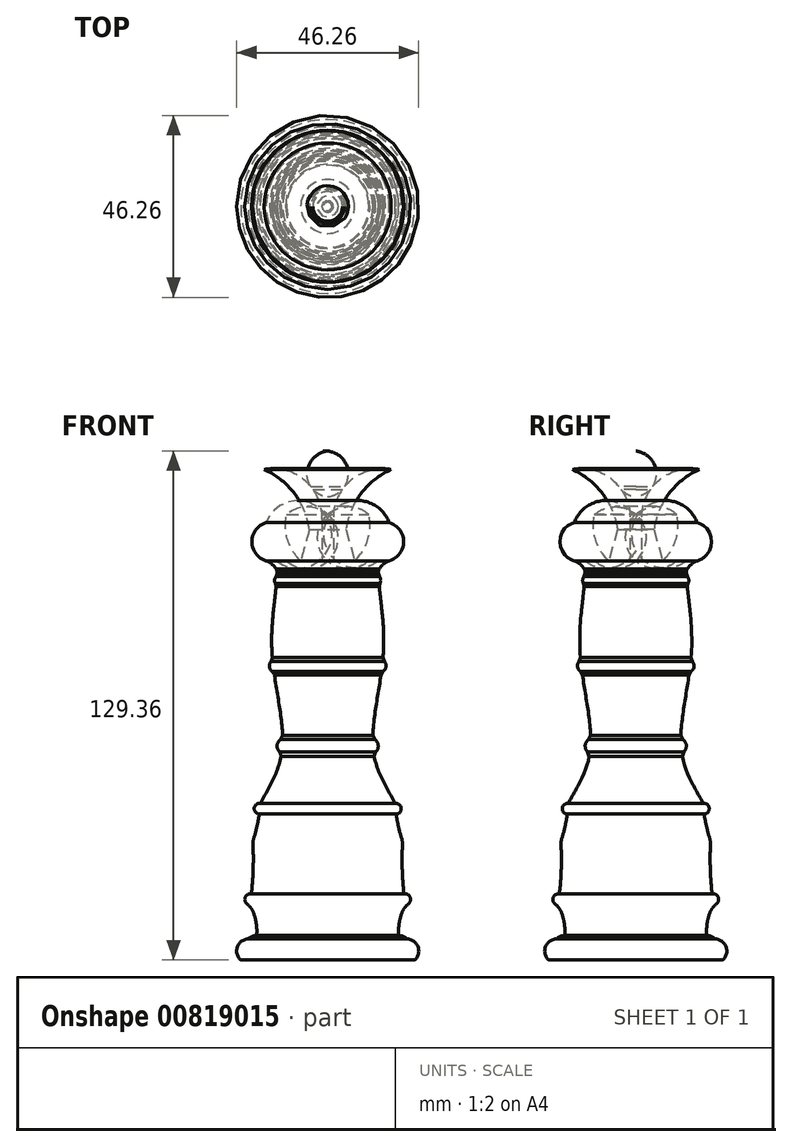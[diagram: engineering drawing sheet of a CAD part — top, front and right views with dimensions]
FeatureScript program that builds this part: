
annotation { "Feature Type Name" : "Feature", "Feature Type Description" : "" }
export const myFeature = defineFeature(function(context is Context, id is Id, definition is map)
    precondition{}
    {
        {
            var Q0;
            Q0=qCreatedBy(makeId("Front.planeOp"),FACE);
            var sketch = newSketch(context, id + "F0", { "sketchPlane" : qUnion([Q0])});
            skLineSegment(sketch, "E0", {"start": v(0, -37.92) * mm, "end": v(0, 57.3) * mm});
            skArc(sketch, "E1", {"start": v(-11.45, 12.13) * mm, "mid": v(-12.85, 10.36) * mm, "end": v(-11.68, 8.42) * mm});
            skArc(sketch, "E2", {"start": v(-14, 32.07) * mm, "mid": v(-14.81, 30.39) * mm, "end": v(-13.62, 28.94) * mm});
            skArc(sketch, "E3", {"start": v(-19.74, -30.2) * mm, "mid": v(-18.98, -22.08) * mm, "end": v(-19.03, -13.92) * mm});
            skFitSpline(sketch, "E4.trimOffspring", {"points": [v(-25.61, -37.92) * mm, v(-19.46, -8.96) * mm, v(-11.68, 8.42) * mm, v(-14.2, 35.39) * mm, v(-12.94, 57.3) * mm, v(-15.84, 63.8) * mm], "startDerivative": vector(16.77, 129.7) * mm, "endDerivative": vector(-31.89, 45.75) * mm});
            skArc(sketch, "E5", {"start": v(-19.03, -13.92) * mm, "mid": v(-17.75, -9.2) * mm, "end": v(-17.15, -4.34) * mm});
            skArc(sketch, "E6", {"start": v(-18.05, -37.92) * mm, "mid": v(-18.31, -33.93) * mm, "end": v(-19.74, -30.2) * mm});
            skArc(sketch, "E7", {"start": v(-17.15, -4.34) * mm, "mid": v(-18.67, -5.58) * mm, "end": v(-17.4, -7.09) * mm});
            skArc(sketch, "E8", {"start": v(-19.38, -27.31) * mm, "mid": v(-21.06, -28.56) * mm, "end": v(-19.74, -30.2) * mm});
            skArc(sketch, "E9", {"start": v(-18.05, -37.92) * mm, "mid": v(-21.18, -41.05) * mm, "end": v(-18.05, -44.17) * mm});
            skArc(sketch, "E10", {"start": v(-20.2, -38.78) * mm, "mid": v(-22.96, -40.84) * mm, "end": v(-22.07, -44.17) * mm});
            skLineSegment(sketch, "E11", {"start": v(-18.05, -44.17) * mm, "end": v(0, -44.17) * mm});
            skLineSegment(sketch, "E12", {"start": v(0, -44.17) * mm, "end": v(0, -37.92) * mm});
            skLineSegment(sketch, "E13", {"start": v(-18.05, -44.17) * mm, "end": v(-22.07, -44.17) * mm});
            skPoint(sketch, "E14.orphan", {"position": v(0, 63.8) * mm});
            skArc(sketch, "E15", {"start": v(-12.4, 50.83) * mm, "mid": v(-12.77, 54.68) * mm, "end": v(-15.62, 57.3) * mm});
            skLineSegment(sketch, "E16", {"start": v(-12.4, 50.83) * mm, "end": v(-13.67, 45.68) * mm});
            skPoint(sketch, "E16.startSnap0", {"position": v(-12.4, 53.75) * mm});
            skArc(sketch, "E17", {"start": v(-12.4, 53.75) * mm, "mid": v(-13.49, 52.3) * mm, "end": v(-12.4, 50.83) * mm});
            skArc(sketch, "E18", {"start": v(-15.62, 66.98) * mm, "mid": v(-19.28, 62.14) * mm, "end": v(-15.62, 57.3) * mm});
            skArc(sketch, "E19", {"start": v(-15.62, 66.98) * mm, "mid": v(-15.84, 61.7) * mm, "end": v(-12.94, 57.3) * mm});
            skLineSegment(sketch, "E20", {"start": v(0, 67.93) * mm, "end": v(0, 57.3) * mm});
            skLineSegment(sketch, "E21.trimOffspring", {"start": v(-7.95, 57.3) * mm, "end": v(0, 57.3) * mm});
            skLineSegment(sketch, "E22", {"start": v(-12.94, 57.3) * mm, "end": v(-7.95, 57.3) * mm});
            skArc(sketch, "E23", {"start": v(-10.44, 69.01) * mm, "mid": v(-13.06, 63.15) * mm, "end": v(-10.44, 57.3) * mm});
            skPoint(sketch, "E23.startSnap0", {"position": v(-10.44, 57.3) * mm});
            skArc(sketch, "E24", {"start": v(-10.44, 69.01) * mm, "mid": v(-10.21, 62.68) * mm, "end": v(-6.86, 57.3) * mm});
            skArc(sketch, "E25", {"start": v(-1.43, 67.73) * mm, "mid": v(-5.73, 77.63) * mm, "end": v(-16.14, 80.49) * mm});
            skArc(sketch, "E26", {"start": v(-4.64, 65.2) * mm, "mid": v(-8.41, 74.33) * mm, "end": v(-16.14, 80.49) * mm});
            skArc(sketch, "E27", {"start": v(0, 85.16) * mm, "mid": v(-5.24, 79.36) * mm, "end": v(0, 73.56) * mm});
            skLineSegment(sketch, "E28", {"start": v(0, 85.16) * mm, "end": v(0, 73.56) * mm});
            skLineSegment(sketch, "E29", {"start": v(-4.64, 65.2) * mm, "end": v(-6.86, 57.3) * mm});
            skLineSegment(sketch, "E30", {"start": v(-1.43, 67.73) * mm, "end": v(-1.43, 57.3) * mm});
            skSolve(sketch);
        }
        {
            var Q0;
            Q0=qSketchRegion(id+"F0",true);
            var Q1;
            Q1=sQuery(id+"F0.wireOp",EDGE,"E0");
            revolve(context, id + "F1", {"surfaceOperationType" : NewSurfaceOperationType.NEW, "entities" : qUnion([Q0]), "axis" : qUnion([Q1]), "revolveType" : RevolveType.FULL});
        }
        {
            var Q0;
            Q0=makeQuery(id+"F1.opRevolve","SWEPT_EDGE",EDGE,{"disambiguationData":[OSD([sQuery(id+"F0.wireOp",EDGE,"VEvPsMBn-cbsM-wzOz-HuDP-UBSZChaoLJEj"),sQuery(id+"F0.wireOp",EDGE,"E4.trimOffspring")])]});
            chamfer(context, id + "F2", {"entities" : qUnion([Q0]), "width" : 1.27 * mm, "tangentPropagation" : true});
        }
        {
            var Q0;
            Q0=makeQuery(id+"F1.opRevolve","SWEPT_EDGE",EDGE,{"disambiguationData":[OSD([sQuery(id+"F0.wireOp",EDGE,"E3"),sQuery(id+"F0.wireOp",EDGE,"E6")])]});
            var Q1;
            Q1=makeQuery(id+"F1.opRevolve","SWEPT_EDGE",EDGE,{"disambiguationData":[OSD([sQuery(id+"F0.wireOp",EDGE,"E3"),sQuery(id+"F0.wireOp",EDGE,"E5")])]});
            fillet(context, id + "F3", {"entities" : qUnion([Q0, Q1]), "radius" : 5.08 * mm, "tangentPropagation" : true, "allowEdgeOverflow" : false});
        }
    });
